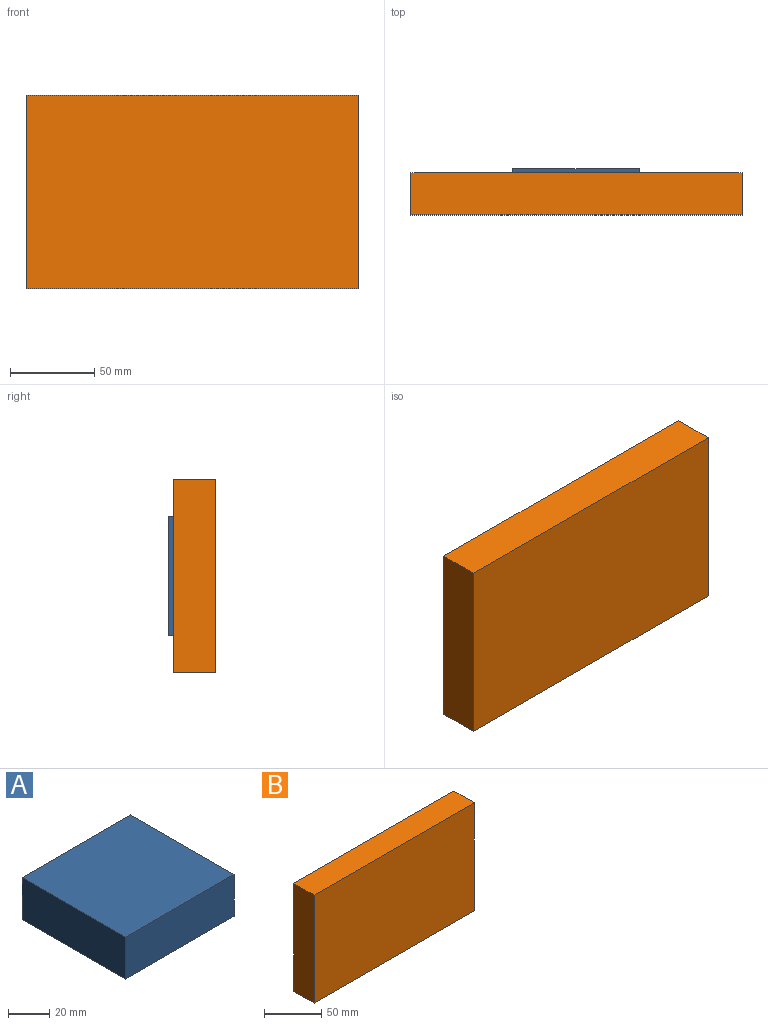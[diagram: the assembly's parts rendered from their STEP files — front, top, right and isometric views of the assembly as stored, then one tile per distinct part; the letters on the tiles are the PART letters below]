
ASSEMBLY  parts=2 mates=1
PART A: 6 faces, bbox 74.9x71.1x25 mm
  f0: plane 74.92x25mm, normal (0,-1,0), area 1873mm2, adj f1,f3,f4,f5
  f1: plane 71.15x25mm, normal (1,0,0), area 1778.7mm2, adj f0,f2,f4,f5
  f2: plane 74.92x25mm, normal (0,1,0), area 1873mm2, adj f1,f3,f4,f5
  f3: plane 71.15x25mm, normal (-1,0,0), area 1778.7mm2, adj f0,f2,f4,f5
  f4: plane 74.92x71.15mm, normal (0,0,1), area 5330.4mm2, adj f0,f1,f2,f3
  f5: plane 74.92x71.15mm, normal (0,0,-1), area 5330.4mm2, adj f0,f1,f2,f3
PART B: 11 faces, bbox 197.3x25x115.1 mm
  f0: plane 197.34x115.11mm, normal (0,1,0), area 1537.3mm2, adj f1,f2,f3,f4,f6,f7,f8,f9
  f1: plane 197.34x25mm, normal (0,0,1), area 4933.6mm2, adj f0,f2,f4,f5
  f2: plane 115.11x25mm, normal (-1,0,0), area 2877.8mm2, adj f0,f1,f3,f5
  f3: plane 197.34x25mm, normal (0,0,-1), area 4933.6mm2, adj f0,f2,f4,f5
  f4: plane 115.11x25mm, normal (1,0,0), area 2877.8mm2, adj f0,f1,f3,f5
  f5: plane 197.34x115.11mm, normal (0,-1,0), area 22716.7mm2, adj f1,f2,f3,f4
  f6: plane 192.34x22.5mm, normal (0,0,-1), area 4327.8mm2, adj f0,f7,f9,f10
  f7: plane 110.11x22.5mm, normal (1,0,0), area 2477.5mm2, adj f0,f6,f8,f10
  f8: plane 192.34x22.5mm, normal (0,0,1), area 4327.8mm2, adj f0,f7,f9,f10
  f9: plane 110.11x22.5mm, normal (-1,0,0), area 2477.5mm2, adj f0,f6,f8,f10
  f10: plane 192.34x110.11mm, normal (0,1,0), area 21179.5mm2, adj f6,f7,f8,f9
PLACE A rot(axis=(-1,0,0),90deg) t=(0.01,-10.17,-0.27)mm
PLACE B t=(5.02,12.33,3.32)mm fixed
MATE fastened A.f5 <-> B.f10  axis (0,-1,0) through (0.01,-10.17,-0.27)mm
